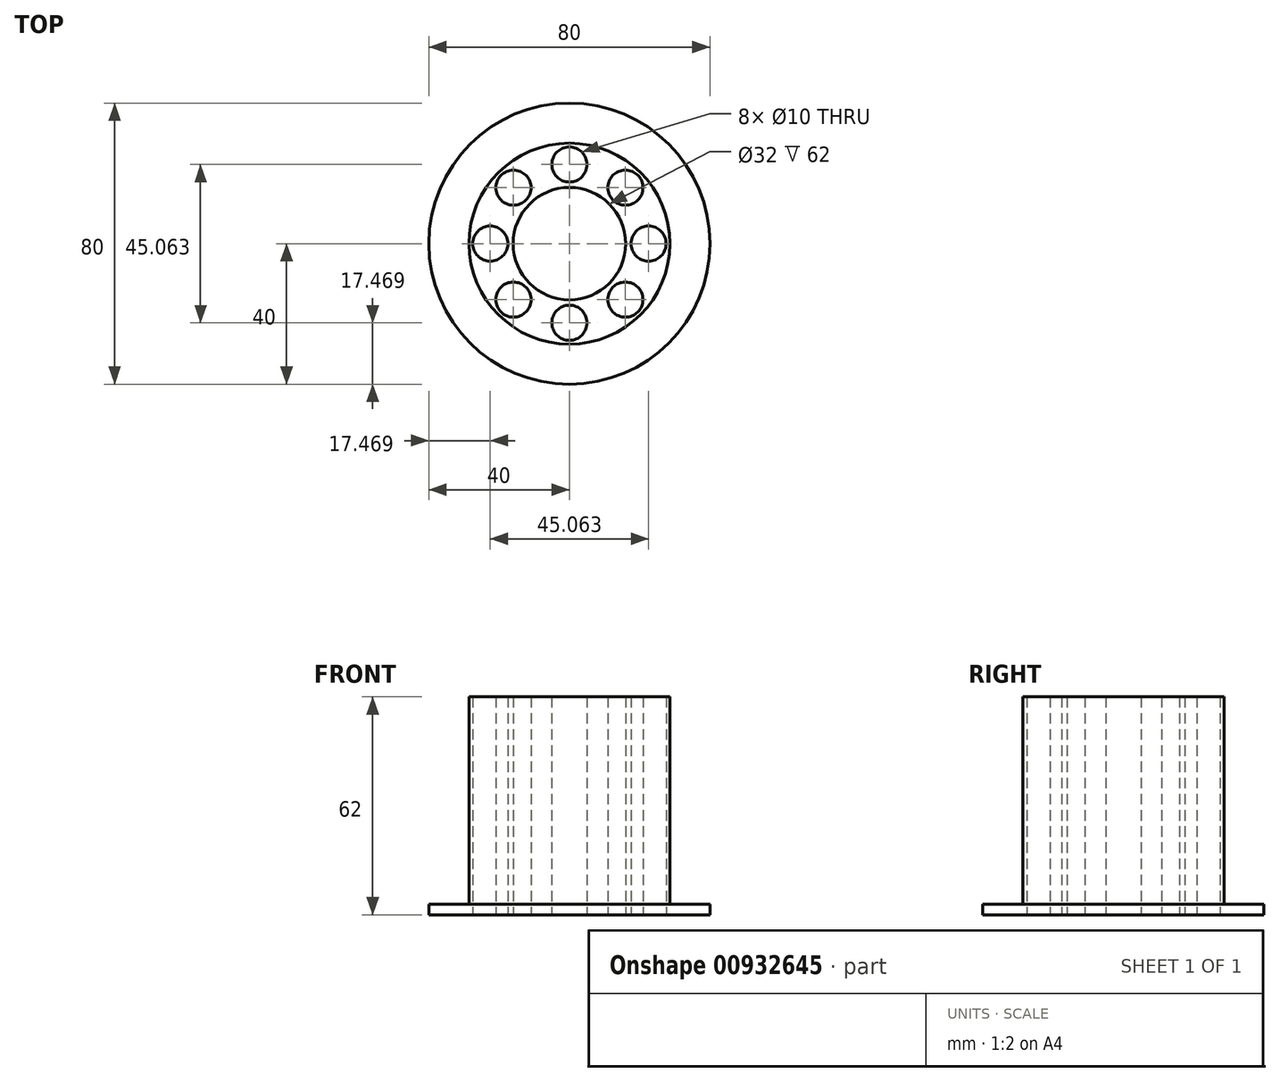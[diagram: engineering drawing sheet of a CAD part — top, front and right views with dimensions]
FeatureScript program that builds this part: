
annotation { "Feature Type Name" : "Feature", "Feature Type Description" : "" }
export const myFeature = defineFeature(function(context is Context, id is Id, definition is map)
    precondition{}
    {
        {
            var Q0;
            Q0=qCreatedBy(makeId("Top.planeOp"),FACE);
            var sketch = newSketch(context, id + "F0", { "sketchPlane" : qUnion([Q0])});
            skCircle(sketch, "E0", {"center": v(0, 0) * mm, "radius": 16 * mm});
            skCircle(sketch, "E1", {"center": v(0, 0) * mm, "radius": 28.6 * mm});
            skCircle(sketch, "E2", {"center": v(0, 0) * mm, "radius": 40 * mm});
            skLineSegment(sketch, "E3", {"start": v(-28.6, 0) * mm, "end": v(-16, 0) * mm, "construction": true});
            skCircle(sketch, "E4", {"center": v(-22.53, 0) * mm, "radius": 5 * mm});
            skCircle(sketch, "E5", {"center": v(0, 22.53) * mm, "radius": 5 * mm});
            skCircle(sketch, "E6", {"center": v(22.53, 0) * mm, "radius": 5 * mm});
            skCircle(sketch, "E7", {"center": v(0, -22.53) * mm, "radius": 5 * mm});
            skCircle(sketch, "E8", {"center": v(-15.93, -15.93) * mm, "radius": 5 * mm});
            skCircle(sketch, "E9", {"center": v(-15.93, 15.93) * mm, "radius": 5 * mm});
            skCircle(sketch, "E10", {"center": v(15.93, 15.93) * mm, "radius": 5 * mm});
            skCircle(sketch, "E11", {"center": v(15.93, -15.93) * mm, "radius": 5 * mm});
            skSolve(sketch);
        }
        {
            var Q0;
            Q0=makeQuery(id+"F0.imprint","IMPRINT",FACE,{"disambiguationData":[TD([[makeQuery(id+"F0.imprint","IMPRINT",EDGE,{"derivedFrom":sQuery(id+"F0.wireOp",EDGE,"E1")}),-1.0]])]});
            extrude(context, id + "F1", {"entities" : qUnion([Q0]), "depth" : 3 * mm, "offsetDistance" : 25 * mm});
        }
        {
            var Q0;
            Q0=makeQuery(id+"F0.imprint","IMPRINT",FACE,{"disambiguationData":[TD([[makeQuery(id+"F0.imprint","IMPRINT",EDGE,{"derivedFrom":sQuery(id+"F0.wireOp",EDGE,"E0")}),-1.0]])]});
            extrude(context, id + "F2", {"entities" : qUnion([Q0]), "operationType" : NewBodyOperationType.ADD, "depth" : 62 * mm, "offsetDistance" : 25 * mm});
        }
    });
